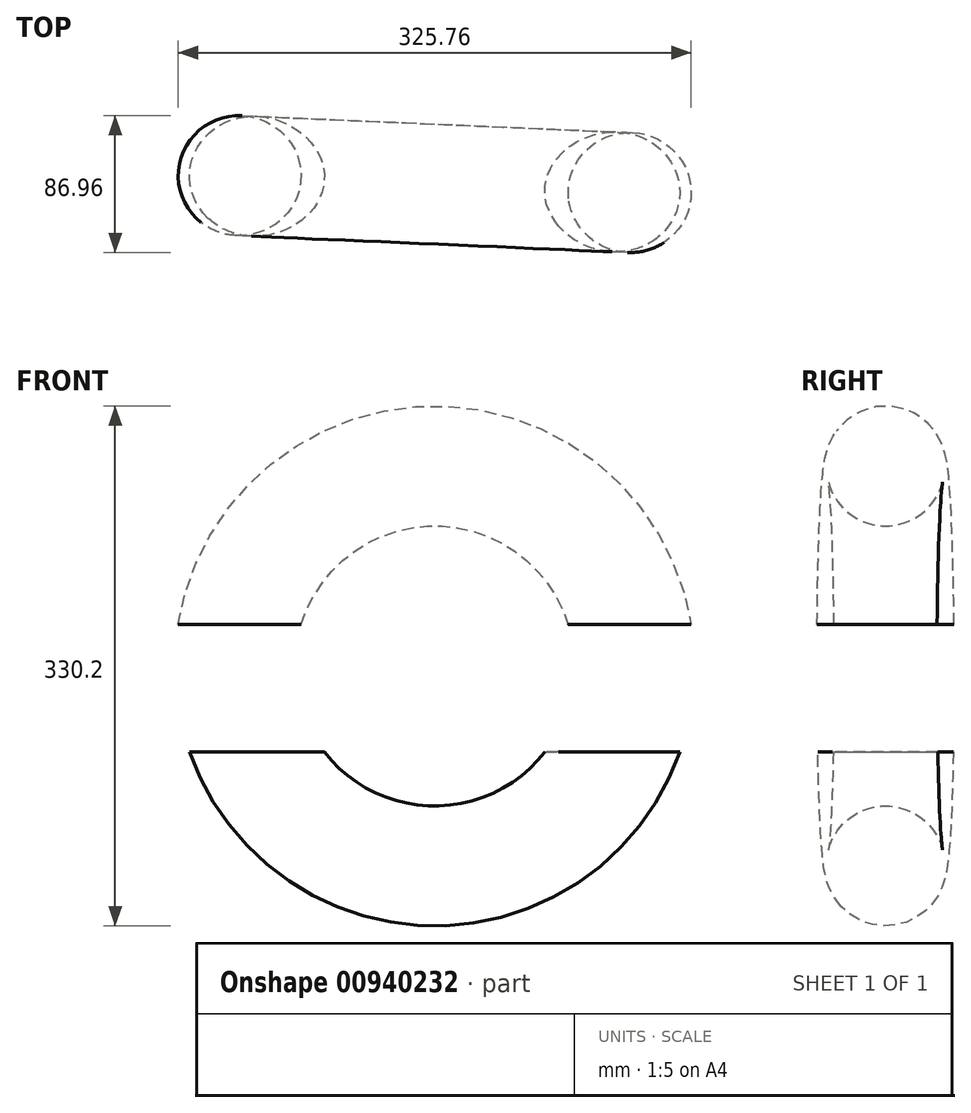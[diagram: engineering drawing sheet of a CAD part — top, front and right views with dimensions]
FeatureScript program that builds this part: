
annotation { "Feature Type Name" : "Feature", "Feature Type Description" : "" }
export const myFeature = defineFeature(function(context is Context, id is Id, definition is map)
    precondition{}
    {
        {
            var Q0;
            Q0=qCreatedBy(makeId("Top.planeOp"),FACE);
            var sketch = newSketch(context, id + "F0", { "sketchPlane" : qUnion([Q0])});
            skCircle(sketch, "E0", {"center": v(-175.46, -23.45) * mm, "radius": 38.1 * mm});
            skCircle(sketch, "E1", {"center": v(-187.06, -37.14) * mm, "radius": 56.04 * mm});
            skSolve(sketch);
        }
        {
            var Q0;
            Q0=qCreatedBy(makeId("Top.planeOp"),FACE);
            var sketch = newSketch(context, id + "F1", { "sketchPlane" : qUnion([Q0])});
            skLineSegment(sketch, "E2", {"start": v(-52.58, -121.3) * mm, "end": v(-41.6, 132.46) * mm});
            skSolve(sketch);
        }
        {
            var Q0;
            Q0=makeQuery(id+"F0.imprint","IMPRINT",FACE,{"disambiguationData":[TD([[makeQuery(id+"F0.imprint","IMPRINT",EDGE,{"derivedFrom":sQuery(id+"F0.wireOp",EDGE,"2FX0rYuT-smHs-s0rB-iBou-tfQBacWrvHI1")}),-1.0]])]});
            var Q1;
            Q1=makeQuery(id+"F0.imprint","IMPRINT",FACE,{"disambiguationData":[TD([[makeQuery(id+"F0.imprint","IMPRINT",EDGE,{"derivedFrom":sQuery(id+"F0.wireOp",EDGE,"E0")}),1.0]])]});
            var Q2;
            Q2=sQuery(id+"F1.wireOp",EDGE,"E2");
            revolve(context, id + "F2", {"surfaceOperationType" : NewSurfaceOperationType.NEW, "entities" : qUnion([Q0, Q1]), "axis" : qUnion([Q2]), "revolveType" : RevolveType.FULL});
        }
        {
            var Q0;
            Q0=qCreatedBy(makeId("Right.planeOp"),FACE);
            var sketch = newSketch(context, id + "F3", { "sketchPlane" : qUnion([Q0])});
            skLineSegment(sketch, "E3.bottom", {"start": v(61.8, 26.28) * mm, "end": v(-118.54, 26.28) * mm});
            skLineSegment(sketch, "E3.top", {"start": v(61.8, -54.73) * mm, "end": v(-118.54, -54.73) * mm});
            skLineSegment(sketch, "E3.left", {"start": v(61.8, 26.28) * mm, "end": v(61.8, -54.73) * mm});
            skLineSegment(sketch, "E3.right", {"start": v(-118.54, 26.28) * mm, "end": v(-118.54, -54.73) * mm});
            skSolve(sketch);
        }
        {
            var Q0;
            Q0 = qSketchRegion(id + "F3", true);
            extrude(context, id + "F4", {"entities" : qUnion([Q0]), "operationType" : NewBodyOperationType.REMOVE, "endBound" : BoundingType.SYMMETRIC, "depth" : 508 * mm, "offsetDistance" : 25.4 * mm});
        }
    });
